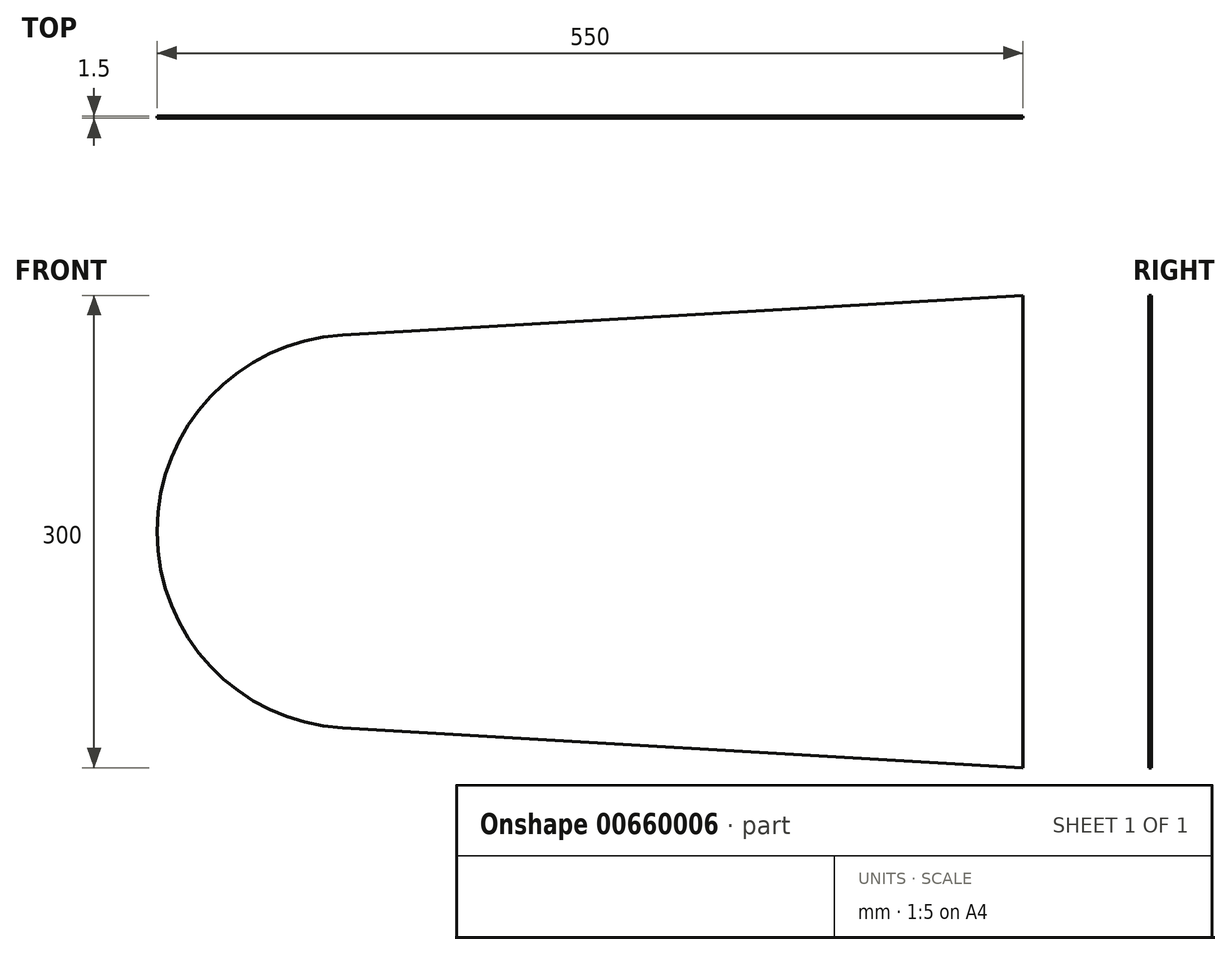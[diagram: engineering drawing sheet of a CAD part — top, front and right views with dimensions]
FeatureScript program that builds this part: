
annotation { "Feature Type Name" : "Feature", "Feature Type Description" : "" }
export const myFeature = defineFeature(function(context is Context, id is Id, definition is map)
    precondition{}
    {
        {
            var Q0;
            Q0=qCreatedBy(makeId("Front.planeOp"),FACE);
            var sketch = newSketch(context, id + "F0", { "sketchPlane" : qUnion([Q0])});
            skCircle(sketch, "E0", {"center": v(-425, 0) * mm, "radius": 125 * mm});
            skLineSegment(sketch, "E1", {"start": v(0, 0) * mm, "end": v(-910.58, 0) * mm});
            skLineSegment(sketch, "E2", {"start": v(0, 150) * mm, "end": v(-432.28, 124.79) * mm});
            skLineSegment(sketch, "E3", {"start": v(0, -150) * mm, "end": v(-432.28, -124.79) * mm});
            skLineSegment(sketch, "E4", {"start": v(0, 0) * mm, "end": v(0, 150) * mm});
            skLineSegment(sketch, "E5", {"start": v(0, 0) * mm, "end": v(0, -150) * mm});
            skSolve(sketch);
        }
        {
            var Q0;
            {var subQ0=sQuery(id+"F0.wireOp",EDGE,"E1");var subQ1=sQuery(id+"F0.wireOp",EDGE,"ZFQ2gco3-H9qs-s49o-krYr-cHRq3sGXDUtx");var subQ2=makeQuery(id+"F0.imprint","INTERSECT",VERTEX,{"derivedFrom":[subQ1,subQ0]});Q0=makeQuery(id+"F0.imprint","IMPRINT",FACE,{"disambiguationData":[TD([[makeQuery(id+"F0.imprint","IMPRINT",EDGE,{"disambiguationData":[TD([[subQ2,-1.0]])],"derivedFrom":subQ1}),-1.0]])]});}
            var Q1;
            {var subQ0=sQuery(id+"F0.wireOp",EDGE,"E2");var subQ1=sQuery(id+"F0.wireOp",EDGE,"ZFQ2gco3-H9qs-s49o-krYr-cHRq3sGXDUtx");var subQ7=makeQuery(id+"F0.imprint","INTERSECT",VERTEX,{"disambiguationData":[OD(1.0)],"derivedFrom":[subQ1,subQ0]});Q1=makeQuery(id+"F0.imprint","IMPRINT",FACE,{"disambiguationData":[TD([[makeQuery(id+"F0.imprint","IMPRINT",EDGE,{"disambiguationData":[TD([[subQ7,-1.0]])],"derivedFrom":subQ1}),1.0]])]});}
            var Q2;
            {var subQ0=sQuery(id+"F0.wireOp",EDGE,"E2");var subQ1=sQuery(id+"F0.wireOp",EDGE,"ZFQ2gco3-H9qs-s49o-krYr-cHRq3sGXDUtx");var subQ2=makeQuery(id+"F0.imprint","INTERSECT",VERTEX,{"disambiguationData":[OD(1.0)],"derivedFrom":[subQ1,subQ0]});Q2=makeQuery(id+"F0.imprint","IMPRINT",FACE,{"disambiguationData":[TD([[makeQuery(id+"F0.imprint","IMPRINT",EDGE,{"disambiguationData":[TD([[subQ2,-1.0]])],"derivedFrom":subQ1}),-1.0]])]});}
            var Q3;
            {var subQ0=sQuery(id+"F0.wireOp",EDGE,"E0");var subQ1=makeQuery(id+"F0.imprint","INTERSECT",VERTEX,{"derivedFrom":[subQ0,sQuery(id+"F0.wireOp",EDGE,"E3")]});Q3=makeQuery(id+"F0.imprint","IMPRINT",FACE,{"disambiguationData":[TD([[makeQuery(id+"F0.imprint","IMPRINT",EDGE,{"disambiguationData":[TD([[subQ1,1.0]])],"derivedFrom":subQ0}),1.0]])]});}
            var Q4;
            {var subQ0=sQuery(id+"F0.wireOp",EDGE,"E0");var subQ1=makeQuery(id+"F0.imprint","INTERSECT",VERTEX,{"derivedFrom":[subQ0,sQuery(id+"F0.wireOp",EDGE,"E2")]});Q4=makeQuery(id+"F0.imprint","IMPRINT",FACE,{"disambiguationData":[TD([[makeQuery(id+"F0.imprint","IMPRINT",EDGE,{"disambiguationData":[TD([[subQ1,1.0]])],"derivedFrom":subQ0}),1.0]])]});}
            var Q5;
            {var subQ0=sQuery(id+"F0.wireOp",EDGE,"E3");Q5=makeQuery(id+"F0.imprint","IMPRINT",FACE,{"disambiguationData":[TD([[makeQuery(id+"F0.imprint","IMPRINT",EDGE,{"derivedFrom":subQ0}),-1.0]])]});}
            var Q6;
            {var subQ0=sQuery(id+"F0.wireOp",EDGE,"E2");Q6=makeQuery(id+"F0.imprint","IMPRINT",FACE,{"disambiguationData":[TD([[makeQuery(id+"F0.imprint","IMPRINT",EDGE,{"derivedFrom":subQ0}),1.0]])]});}
            extrude(context, id + "F1", {"entities" : qUnion([Q0, Q1, Q2, Q3, Q4, Q5, Q6]), "endBound" : BoundingType.SYMMETRIC, "depth" : 1.5 * mm, "offsetDistance" : 25 * mm});
        }
    });
